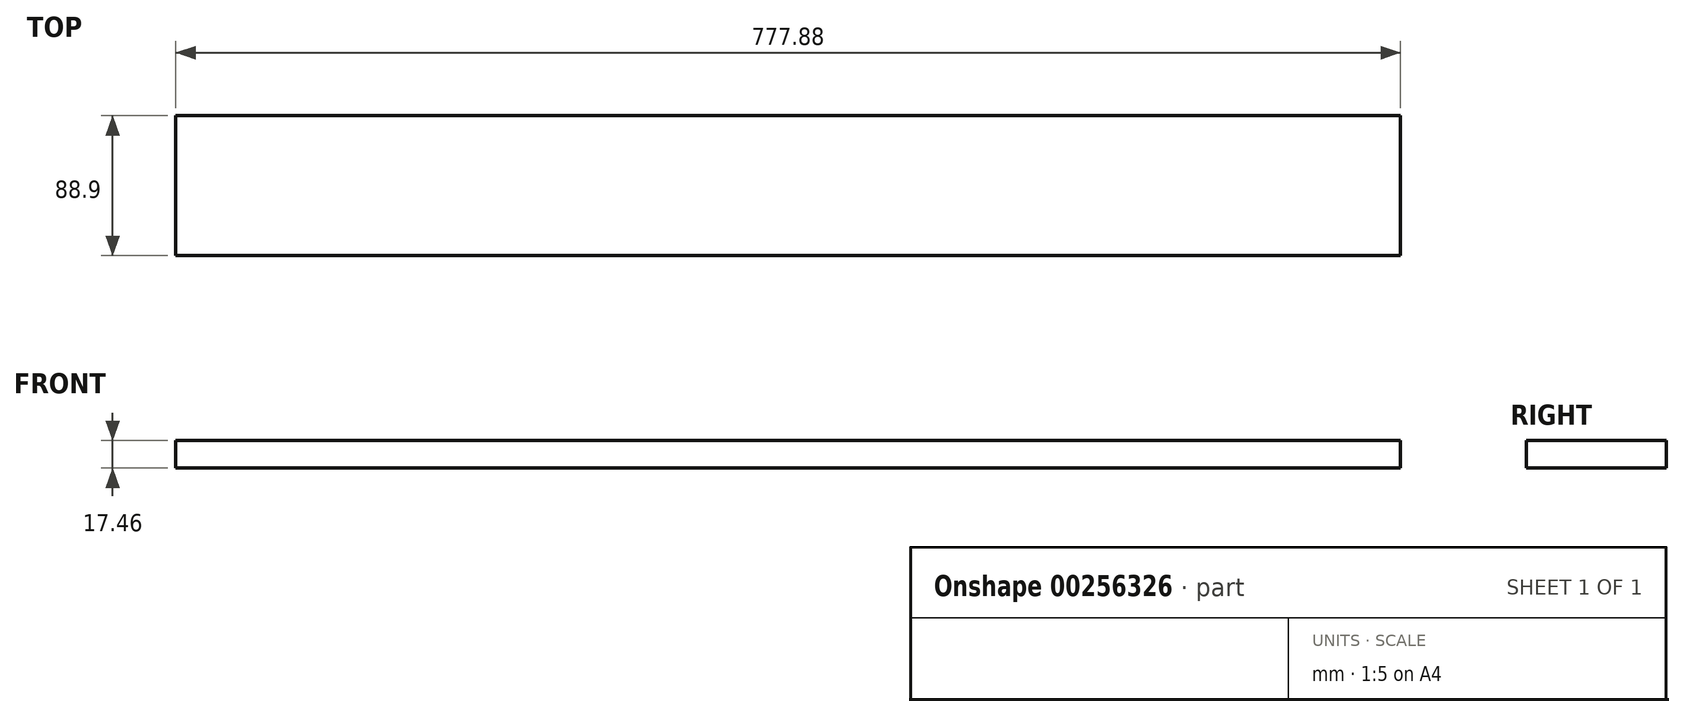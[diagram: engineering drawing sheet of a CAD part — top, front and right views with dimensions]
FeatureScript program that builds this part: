
annotation { "Feature Type Name" : "Feature", "Feature Type Description" : "" }
export const myFeature = defineFeature(function(context is Context, id is Id, definition is map)
    precondition{}
    {
        {
            var Q0;
            Q0=qCreatedBy(makeId("Right.planeOp"),FACE);
            var sketch = newSketch(context, id + "F0", { "sketchPlane" : qUnion([Q0])});
            skLineSegment(sketch, "E0.bottom", {"start": v(-44.45, 8.73) * mm, "end": v(44.45, 8.73) * mm});
            skLineSegment(sketch, "E0.top", {"start": v(-44.45, -8.73) * mm, "end": v(44.45, -8.73) * mm});
            skLineSegment(sketch, "E0.left", {"start": v(-44.45, 8.73) * mm, "end": v(-44.45, -8.73) * mm});
            skLineSegment(sketch, "E0.right", {"start": v(44.45, 8.73) * mm, "end": v(44.45, -8.73) * mm});
            skSolve(sketch);
        }
        {
            var Q0;
            Q0 = qSketchRegion(id + "F0", true);
            extrude(context, id + "F1", {"entities" : qUnion([Q0]), "endBound" : BoundingType.SYMMETRIC, "depth" : 777.88 * mm});
        }
    });
